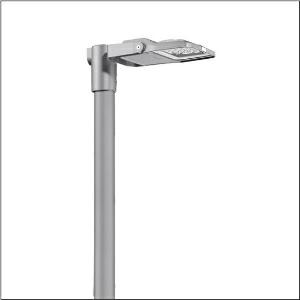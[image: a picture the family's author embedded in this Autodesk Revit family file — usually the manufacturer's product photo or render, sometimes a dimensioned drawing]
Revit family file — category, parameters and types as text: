
# Revit family: floodlight_fl_21_iq_micro___pl33t_5xa7762a2f3a_98d7
name_source: partatom
category: Lighting Fixtures
units: mm (PartAtom-declared; Revit-internal decimal feet)

## family parameters
Cut with Voids When Loaded = No
Host = Face
Light Source = No
Part Type = Normal
Room Calculation Point = No
Round Connector Dimension = Use Diameter
Shared = No

## types (1)
- --- (1 x LED, 2930 lm, 23.1 W, 3000K)
    Apparent Load = 23 VA
    CIE Flux Codes = 26 75 99 100 100
    Color Rendering = 70
    Color Temperature = 3000K
    Default Elevation = 1800 mm
    Description = Floodlight FL 21 iQ micro, floodlight, primary light control with lens, of PMMA, primary optical cover: protective disc, of toughened safety glass, transparent, light distribution: PL33T, light emission: direct distribution, installation type: surface-mounted, LED, High Power LED, rated luminous flux: 2.930lm, luminous efficacy: 127lm/W, light colour: 730, colour temperature: 3000K, control: Auto-Match, Temp-Guard, Night-Set, Smart-Wire, Desk-Remote (wireless, voltage-free reading and setting of iQ features in the workshop via application-optimized NFC function/RFID function), optimised constant luminous flux control (CLO 2.0), Street-Remote, with terminal, 6-pole, mains connection: 220..240V, AC, 50/60Hz, start of lifetime: 23W, end of service life: 24W, reduction: 11W, luminaire housing, of diecast aluminium, powder-coated, Siteco® metallic grey (DB 702S), corrosivity category C5 mid according to DIN EN ISO 12944, sealing non-destructively replaceable, please order mast flange separately, mast bracket, of steel, galvanised, powder-coated, Siteco® metallic grey (DB 702S), protection rating (complete): IP66, insulation class (complete): insulation class II (safety insulation), certification: CE, ENEC, VDE, protection symbol: D, impact resistance: IK07, permissible operating ambient temperature: -40..+40°C, permissible operating ambient temperature for outdoor applications: -40..+50°C, standard: DIN EN 12944, LABS conformity tested according to VDMA 24364:2018-05, packaging unit: 1 piece

Light Distribution: PL33T
    Height = 65 mm
    Lamp = 1 x LED
    Lamp Light Flux = 2930 lm
    Lamp Power = 23.1 W
    Lamp count = 1
    Length = 312 mm
    Luminous efficacy = 127 lm/W
    Manufacturer = Siteco
    ModVariant = No
    Model = 5XA7762A2F3A
    Number of Poles = 1
    OnlyDefault = Yes
    Power Factor = 1
    Product Name = Floodlight FL 21 iQ micro | PL33T
    Product group = floodlight | pylon annexe
    ProductGroupID = 6200
    Protection Class = Protection class II
    Protection Degree = IP 66
    RLX_Detail_Level = 1
    RLX_Emergency_Light_Flux = 0 lm
    RLX_Emergency_Type = 0
    RLX_Emergency_Type_DB = No
    RlxData = <blob elided: 101697 chars, md5=f7de8e64>
    Socket = socket
    Standby Power = 0 W
    System Light Flux = 2930 lm
    System Power = 23 W
    Type Comments = factory setting: luminous flux: 100 % | dim-lin: 254 | 455 mA
    Type Image = l_1007121.jpg
    URL = http://relux.com
    VarID = @adj_098131
    Voltage = 0 V
    Weight = 0.00 kg
    Width = 230 mm

## geometry (parser evidence)
native form markers: Blend x4, Sweep x13
no freeform markers — native parametric forms only
